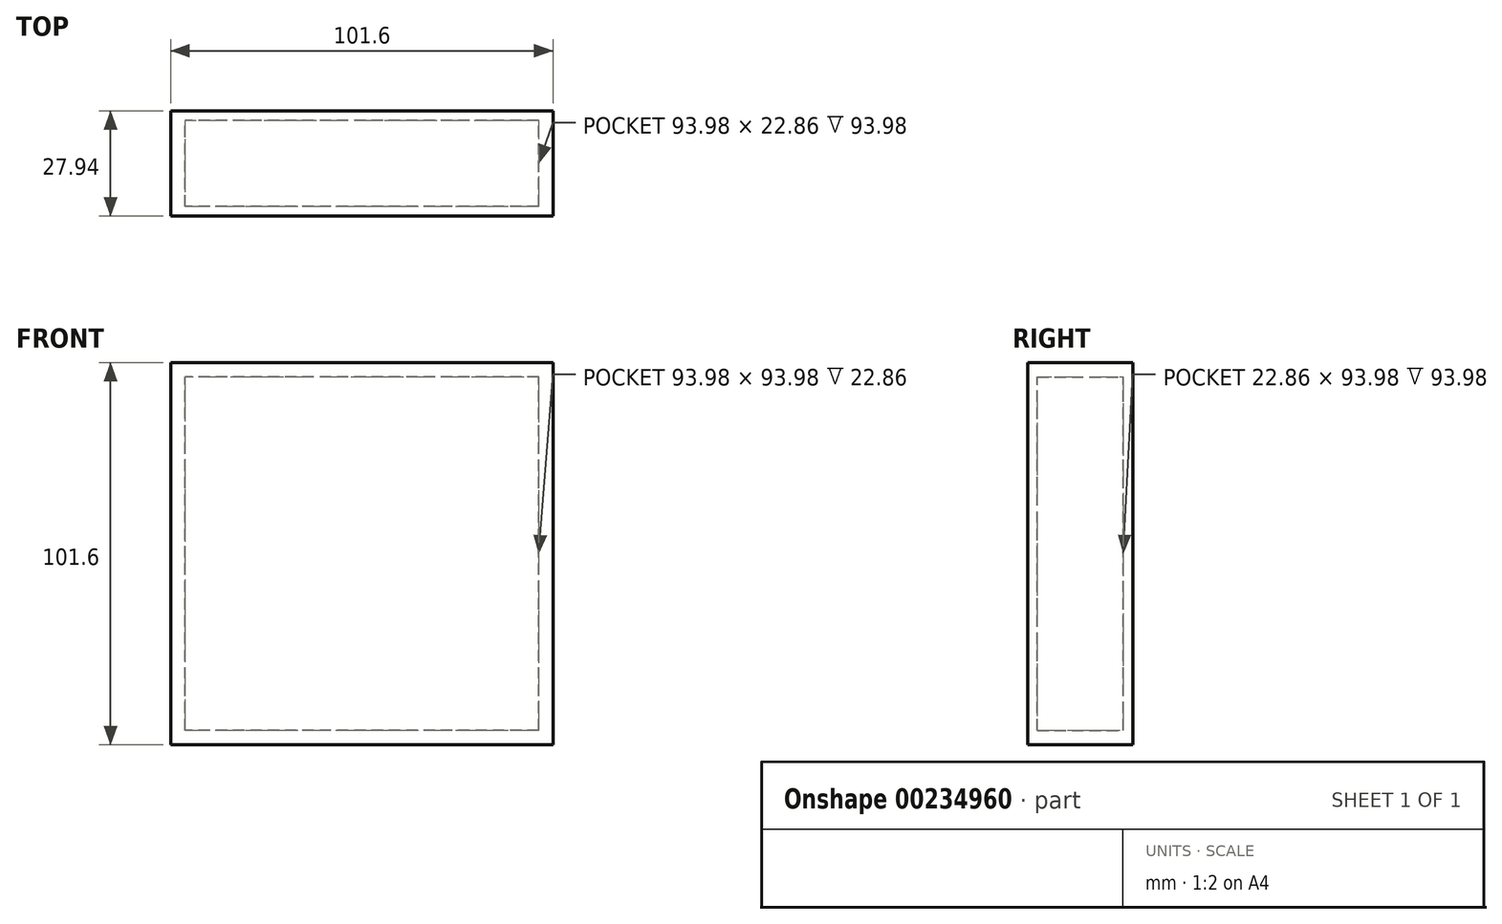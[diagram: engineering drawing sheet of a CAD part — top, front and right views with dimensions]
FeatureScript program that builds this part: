
annotation { "Feature Type Name" : "Feature", "Feature Type Description" : "" }
export const myFeature = defineFeature(function(context is Context, id is Id, definition is map)
    precondition{}
    {
        {
            var Q0;
            Q0=qCreatedBy(makeId("Front.planeOp"),FACE);
            var sketch = newSketch(context, id + "F0", { "sketchPlane" : qUnion([Q0])});
            skLineSegment(sketch, "E0.bottom", {"start": v(50.8, -50.8) * mm, "end": v(-50.8, -50.8) * mm});
            skLineSegment(sketch, "E0.top", {"start": v(50.8, 50.8) * mm, "end": v(-50.8, 50.8) * mm});
            skLineSegment(sketch, "E0.left", {"start": v(50.8, -50.8) * mm, "end": v(50.8, 50.8) * mm});
            skLineSegment(sketch, "E0.right", {"start": v(-50.8, -50.8) * mm, "end": v(-50.8, 50.8) * mm});
            skPoint(sketch, "E0.middle", {"position": v(0, 0) * mm});
            skSolve(sketch);
        }
        {
            var Q0;
            Q0 = qSketchRegion(id + "F0", true);
            extrude(context, id + "F1", {"entities" : qUnion([Q0]), "depth" : 25.4 * mm});
        }
        {
            var Q0;
            Q0=makeQuery(id+"F1.opExtrude","CAP_FACE",FACE,{"disambiguationData":[OSD([sQuery(id+"F0.wireOp",EDGE,"E0.bottom"),sQuery(id+"F0.wireOp",EDGE,"E0.top"),sQuery(id+"F0.wireOp",EDGE,"E0.left"),sQuery(id+"F0.wireOp",EDGE,"E0.right")])],"isStart":false});
            shell(context, id + "F5", {"entities" : qUnion([Q0]), "thickness" : 2.54 * mm});
        }
        {
            var Q0;
            Q0=makeQuery(id+"F5.opShell","OFFSET_FACE",FACE,{"disambiguationData":[OSD([sQuery(id+"F0.wireOp",EDGE,"E0.bottom"),sQuery(id+"F0.wireOp",EDGE,"E0.top"),sQuery(id+"F0.wireOp",EDGE,"E0.left"),sQuery(id+"F0.wireOp",EDGE,"E0.right")])]});
            var sketch = newSketch(context, id + "F2", { "sketchPlane" : qUnion([Q0])});
            skLineSegment(sketch, "E1.bottom", {"start": v(47, -47) * mm, "end": v(-47, -47) * mm});
            skLineSegment(sketch, "E1.top", {"start": v(47, 47) * mm, "end": v(-47, 47) * mm});
            skLineSegment(sketch, "E1.left", {"start": v(47, -47) * mm, "end": v(47, 47) * mm});
            skLineSegment(sketch, "E1.right", {"start": v(-47, -47) * mm, "end": v(-46.99, 47) * mm});
            skPoint(sketch, "E1.middle", {"position": v(0, 0) * mm});
            skSolve(sketch);
        }
        {
            var Q0;
            Q0=makeQuery(id+"F2.imprint","IMPRINT",FACE,{"disambiguationData":[TD([[makeQuery(id+"F2.imprint","IMPRINT",EDGE,{"derivedFrom":sQuery(id+"F2.wireOp",EDGE,"E1.bottom")}),1.0]])]});
            extrude(context, id + "F3", {"entities" : qUnion([Q0]), "operationType" : NewBodyOperationType.ADD, "depth" : 12.7 * mm});
        }
        {
            var Q0;
            Q0=makeQuery(id+"F3.opExtrude","CAP_FACE",FACE,{"disambiguationData":[OSD([sQuery(id+"F0.wireOp",EDGE,"E0.bottom"),sQuery(id+"F0.wireOp",EDGE,"E0.top"),sQuery(id+"F0.wireOp",EDGE,"E0.left"),sQuery(id+"F0.wireOp",EDGE,"E0.right"),sQuery(id+"F2.wireOp",EDGE,"E1.bottom"),sQuery(id+"F2.wireOp",EDGE,"E1.top"),sQuery(id+"F2.wireOp",EDGE,"E1.left"),sQuery(id+"F2.wireOp",EDGE,"E1.right")])],"isStart":false});
            extrude(context, id + "F6", {"entities" : qUnion([Q0]), "depth" : 12.7 * mm});
        }
        {
            var Q0;
            Q0=makeQuery(id+"F1.opExtrude","CAP_FACE",FACE,{"disambiguationData":[OSD([sQuery(id+"F0.wireOp",EDGE,"E0.bottom"),sQuery(id+"F0.wireOp",EDGE,"E0.top"),sQuery(id+"F0.wireOp",EDGE,"E0.left"),sQuery(id+"F0.wireOp",EDGE,"E0.right")])],"isStart":false});
            var sketch = newSketch(context, id + "F4", { "sketchPlane" : qUnion([Q0])});
            skLineSegment(sketch, "E2.bottom", {"start": v(50.8, -50.8) * mm, "end": v(-50.8, -50.8) * mm});
            skLineSegment(sketch, "E2.top", {"start": v(50.8, 50.8) * mm, "end": v(-50.8, 50.8) * mm});
            skLineSegment(sketch, "E2.left", {"start": v(50.8, -50.8) * mm, "end": v(50.8, 50.8) * mm});
            skLineSegment(sketch, "E2.right", {"start": v(-50.8, -50.8) * mm, "end": v(-50.8, 50.8) * mm});
            skPoint(sketch, "E2.middle", {"position": v(0, 0) * mm});
            skSolve(sketch);
        }
        {
            var Q0;
            Q0 = qSketchRegion(id + "F4", true);
            var Q1;
            {var subQ0=sQuery(id+"F0.wireOp",EDGE,"E0.bottom");Q1=makeQuery(id+"F4.imprint","IMPRINT",FACE,{"disambiguationData":[TD([[makeQuery(id+"F4.imprint","IMPRINT",EDGE,{"derivedFrom":makeQuery(id+"F5.opShell","OFFSET_EDGE",EDGE,{"disambiguationData":[OSD([subQ0]),TDD([makeQuery(id+"F1.opExtrude","CAP_EDGE",EDGE,{"disambiguationData":[OSD([subQ0])],"isStart":false})])]})}),-1.0]])]});}
            extrude(context, id + "F7", {"entities" : qUnion([Q0, Q1]), "operationType" : NewBodyOperationType.ADD, "depth" : 2.54 * mm});
        }
    });
